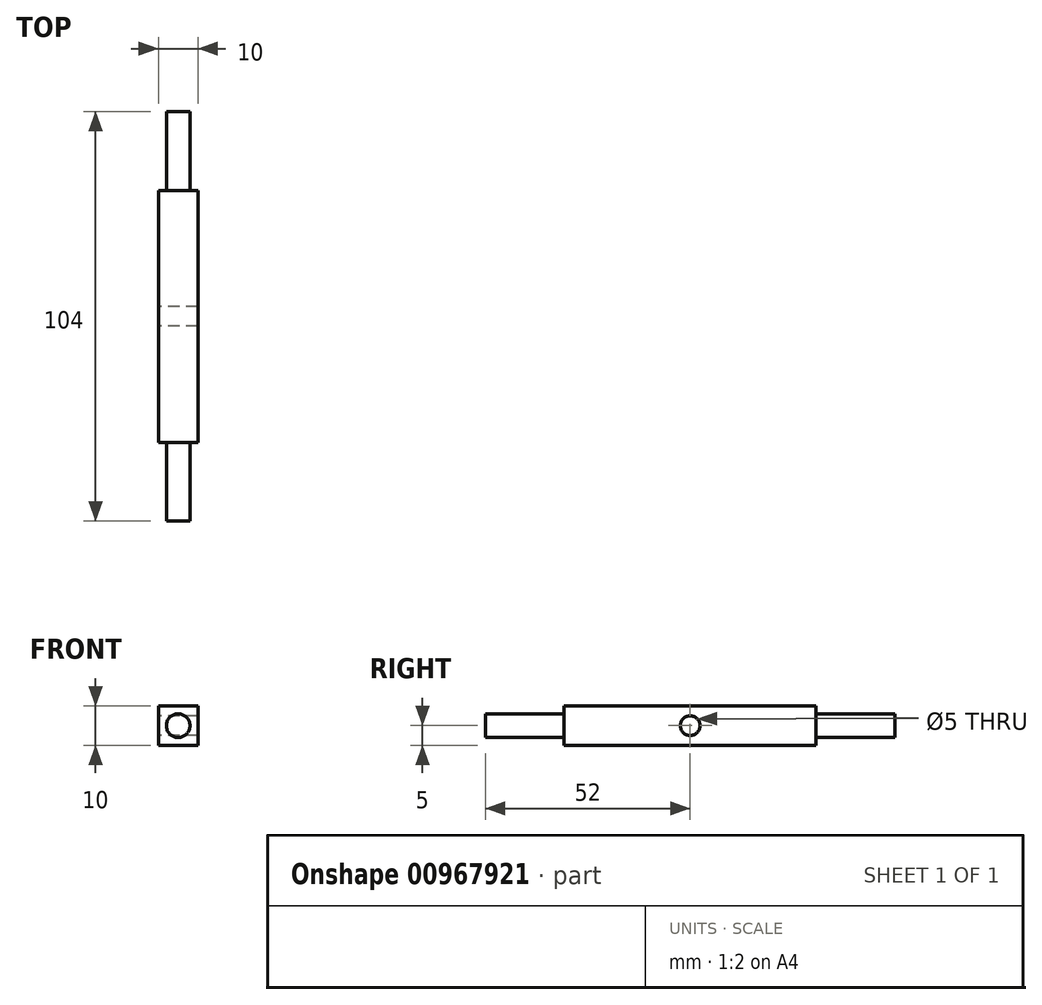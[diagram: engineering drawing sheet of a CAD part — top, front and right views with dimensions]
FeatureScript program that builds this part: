
annotation { "Feature Type Name" : "Feature", "Feature Type Description" : "" }
export const myFeature = defineFeature(function(context is Context, id is Id, definition is map)
    precondition{}
    {
        {
            var Q0;
            Q0=qCreatedBy(makeId("Right.planeOp"),FACE);
            var sketch = newSketch(context, id + "F0", { "sketchPlane" : qUnion([Q0])});
            skLineSegment(sketch, "E0.bottom", {"start": v(-32, 5) * mm, "end": v(32, 5) * mm});
            skLineSegment(sketch, "E0.top", {"start": v(-32, -5) * mm, "end": v(32, -5) * mm});
            skLineSegment(sketch, "E0.left", {"start": v(-32, 5) * mm, "end": v(-32, -5) * mm});
            skLineSegment(sketch, "E0.right", {"start": v(32, 5) * mm, "end": v(32, -5) * mm});
            skPoint(sketch, "E0.middle", {"position": v(0, 0) * mm});
            skCircle(sketch, "E1", {"center": v(0, 0) * mm, "radius": 2.5 * mm});
            skSolve(sketch);
        }
        {
            var Q0;
            Q0=makeQuery(id+"F0.imprint","IMPRINT",FACE,{"disambiguationData":[TD([[makeQuery(id+"F0.imprint","IMPRINT",EDGE,{"derivedFrom":sQuery(id+"F0.wireOp",EDGE,"E0.bottom")}),-1.0]])]});
            extrude(context, id + "F1", {"entities" : qUnion([Q0]), "depth" : 10 * mm, "offsetDistance" : 25 * mm, "symmetric" : true});
        }
        {
            var Q0;
            Q0=qCreatedBy(makeId("Front.planeOp"),FACE);
            var sketch = newSketch(context, id + "F2", { "sketchPlane" : qUnion([Q0])});
            skCircle(sketch, "E2", {"center": v(0, 0) * mm, "radius": 3 * mm});
            skSolve(sketch);
        }
        {
            var Q0;
            Q0 = qSketchRegion(id + "F2", true);
            extrude(context, id + "F3", {"entities" : qUnion([Q0]), "operationType" : NewBodyOperationType.ADD, "depth" : 52 * mm, "offsetDistance" : 25 * mm, "hasSecondDirection" : true, "secondDirectionOppositeDirection" : true, "secondDirectionDepth" : -9 * mm});
        }
        {
            var Q0;
            Q0 = qSketchRegion(id + "F2", true);
            extrude(context, id + "F4", {"entities" : qUnion([Q0]), "operationType" : NewBodyOperationType.ADD, "oppositeDirection" : true, "depth" : 52 * mm, "offsetDistance" : 25 * mm, "hasSecondDirection" : true, "secondDirectionOppositeDirection" : false, "secondDirectionDepth" : -10 * mm});
        }
    });
